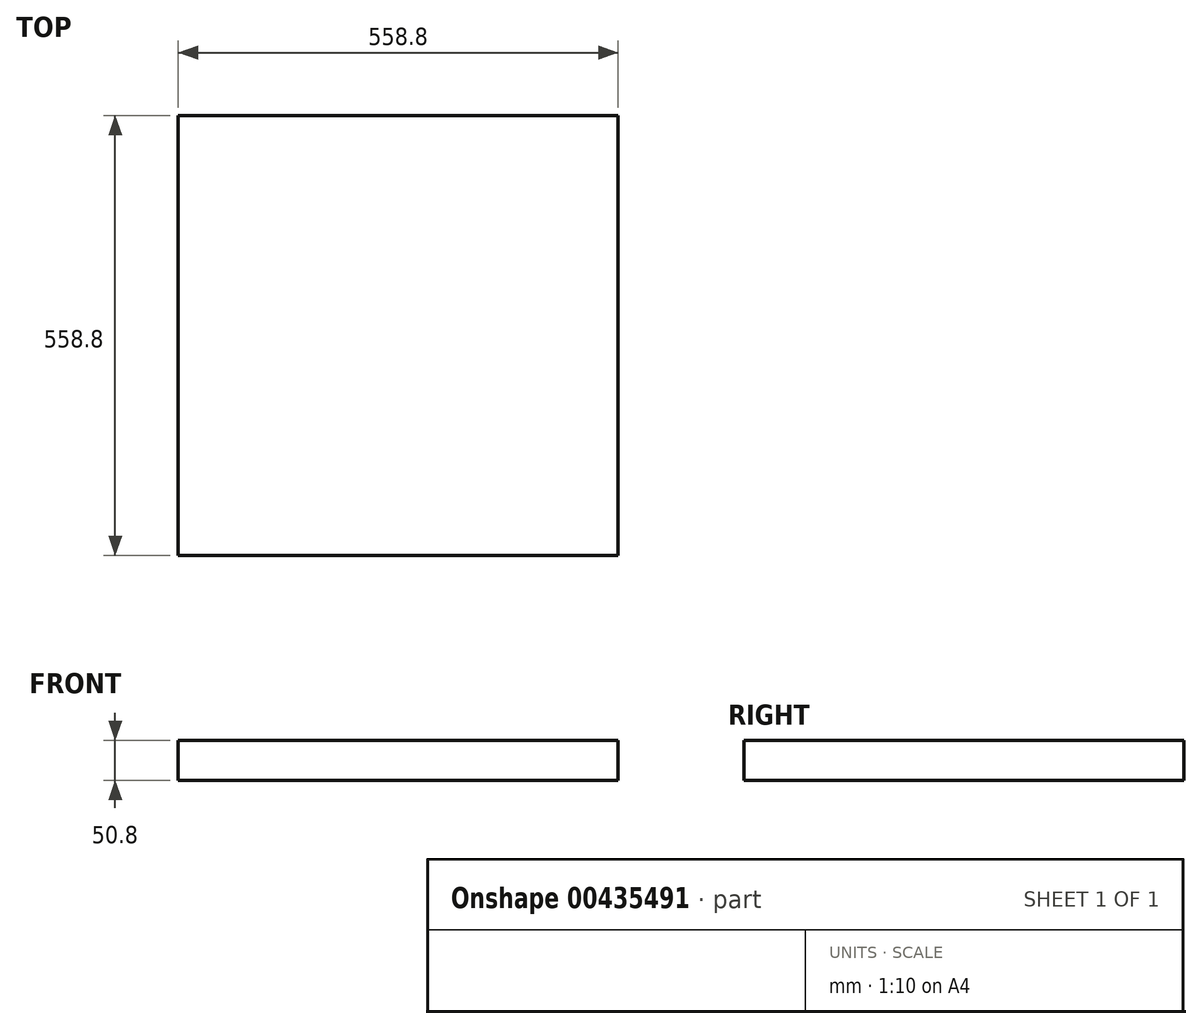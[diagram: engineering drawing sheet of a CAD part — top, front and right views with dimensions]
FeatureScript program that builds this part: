
annotation { "Feature Type Name" : "Feature", "Feature Type Description" : "" }
export const myFeature = defineFeature(function(context is Context, id is Id, definition is map)
    precondition{}
    {
        {
            var Q0;
            Q0=qCreatedBy(makeId("Top.planeOp"),FACE);
            var sketch = newSketch(context, id + "F0", { "sketchPlane" : qUnion([Q0])});
            skLineSegment(sketch, "E0.bottom", {"start": v(279.4, 279.4) * mm, "end": v(-279.4, 279.4) * mm});
            skLineSegment(sketch, "E0.top", {"start": v(279.4, -279.4) * mm, "end": v(-279.4, -279.4) * mm});
            skLineSegment(sketch, "E0.left", {"start": v(279.4, 279.4) * mm, "end": v(279.4, -279.4) * mm});
            skLineSegment(sketch, "E0.right", {"start": v(-279.4, 279.4) * mm, "end": v(-279.4, -279.4) * mm});
            skPoint(sketch, "E0.middle", {"position": v(0, 0) * mm});
            skSolve(sketch);
        }
        {
            var Q0;
            Q0=makeQuery(id+"F0.imprint","IMPRINT",FACE,{"disambiguationData":[TD([[makeQuery(id+"F0.imprint","IMPRINT",EDGE,{"derivedFrom":sQuery(id+"F0.wireOp",EDGE,"E0.bottom")}),1.0]])]});
            extrude(context, id + "F1", {"entities" : qUnion([Q0]), "depth" : 50.8 * mm});
        }
    });
